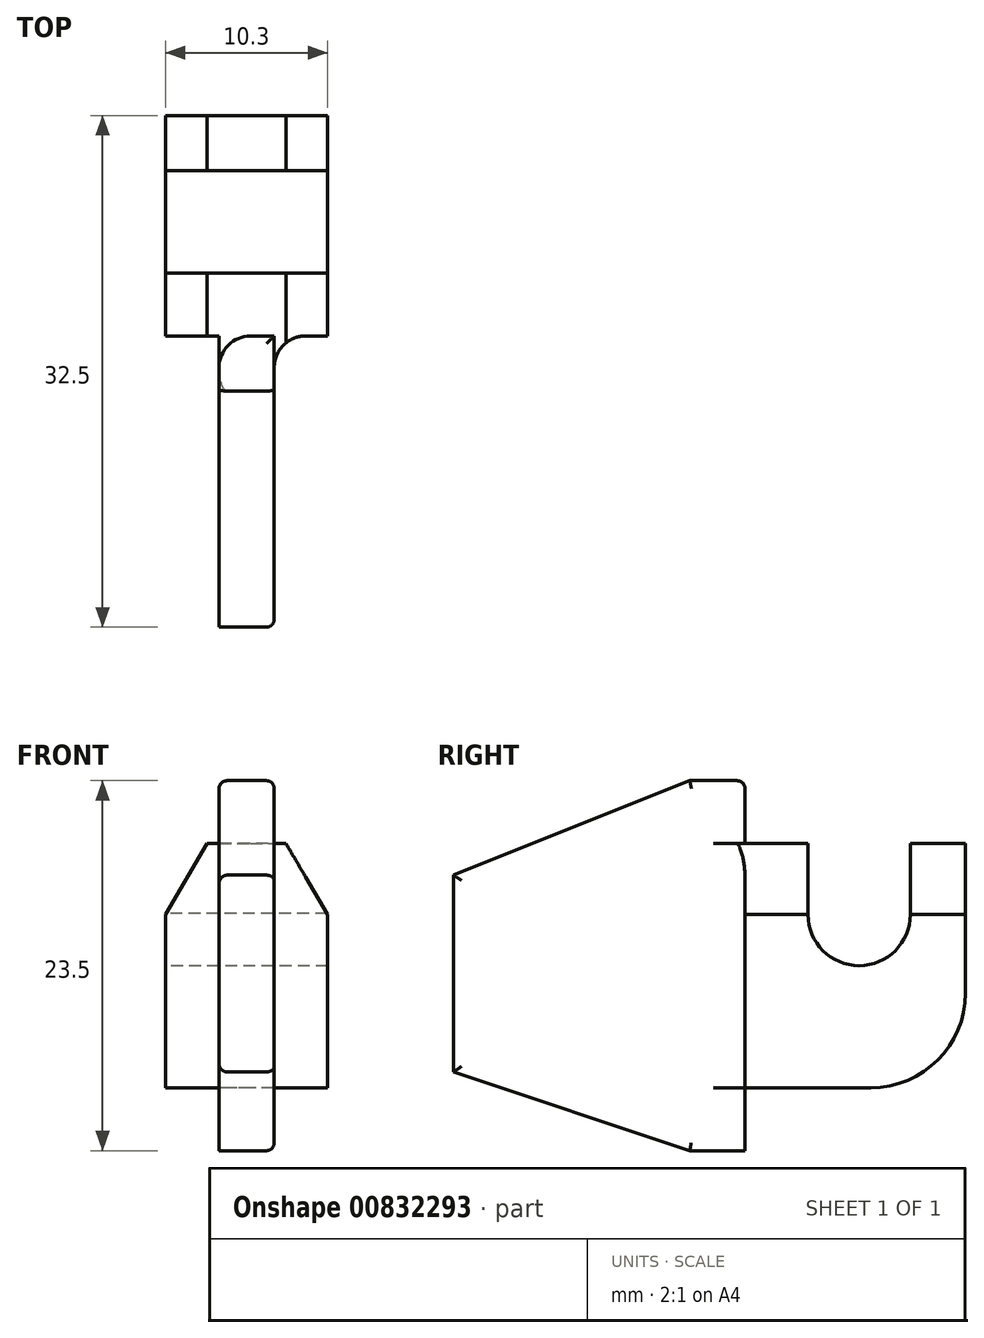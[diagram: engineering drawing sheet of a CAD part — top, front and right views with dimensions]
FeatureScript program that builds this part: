
annotation { "Feature Type Name" : "Feature", "Feature Type Description" : "" }
export const myFeature = defineFeature(function(context is Context, id is Id, definition is map)
    precondition{}
    {
        {
            var Q0;
            Q0=qCreatedBy(makeId("Front.planeOp"),FACE);
            var sketch = newSketch(context, id + "F0", { "sketchPlane" : qUnion([Q0])});
            skLineSegment(sketch, "E0.bottom", {"start": v(5.15, 5.5) * mm, "end": v(-5.15, 5.5) * mm});
            skLineSegment(sketch, "E0.top", {"start": v(5.15, -5.5) * mm, "end": v(-5.15, -5.5) * mm});
            skLineSegment(sketch, "E0.left", {"start": v(5.15, 5.5) * mm, "end": v(5.15, -5.5) * mm});
            skLineSegment(sketch, "E0.right", {"start": v(-5.15, 5.5) * mm, "end": v(-5.15, -5.5) * mm});
            skPoint(sketch, "E0.middle", {"position": v(0, 0) * mm});
            skLineSegment(sketch, "E1", {"start": v(-2.5, 10) * mm, "end": v(2.5, 10) * mm});
            skLineSegment(sketch, "E2", {"start": v(-2.5, 10) * mm, "end": v(-5.15, 5.5) * mm});
            skLineSegment(sketch, "E3", {"start": v(2.5, 10) * mm, "end": v(5.15, 5.5) * mm});
            skLineSegment(sketch, "E4", {"start": v(0, 13.52) * mm, "end": v(0, -10.49) * mm});
            skSolve(sketch);
        }
        {
            var Q0;
            Q0=qSketchRegion(id+"F0",true);
            extrude(context, id + "F1", {"entities" : qUnion([Q0]), "oppositeDirection" : true, "depth" : 14 * mm, "offsetDistance" : 25 * mm});
        }
        {
            var Q0;
            Q0=qCreatedBy(makeId("Right.planeOp"),FACE);
            var sketch = newSketch(context, id + "F2", { "sketchPlane" : qUnion([Q0])});
            skArc(sketch, "E5", {"start": v(4, 5.5) * mm, "mid": v(7.28, 2.25) * mm, "end": v(10.5, 5.57) * mm});
            skLineSegment(sketch, "E6", {"start": v(4, 5.5) * mm, "end": v(4, 10) * mm});
            skLineSegment(sketch, "E7", {"start": v(4, 10) * mm, "end": v(10.5, 10) * mm});
            skLineSegment(sketch, "E8", {"start": v(10.5, 10) * mm, "end": v(10.5, 5.57) * mm});
            skSolve(sketch);
        }
        {
            var Q0;
            Q0=qSketchRegion(id+"F2",true);
            extrude(context, id + "F3", {"entities" : qUnion([Q0]), "operationType" : NewBodyOperationType.REMOVE, "endBound" : BoundingType.THROUGH_ALL, "depth" : 25 * mm, "hasOffset" : true, "offsetDistance" : 50 * mm, "hasSecondDirection" : true, "secondDirectionBound" : SecondDirectionBoundingType.THROUGH_ALL, "secondDirectionOppositeDirection" : true, "secondDirectionDepth" : 50 * mm});
        }
        {
            var Q0;
            Q0=qCreatedBy(makeId("Right.planeOp"),FACE);
            var sketch = newSketch(context, id + "F4", { "sketchPlane" : qUnion([Q0])});
            skLineSegment(sketch, "E9", {"start": v(0, 0) * mm, "end": v(0, 14) * mm});
            skLineSegment(sketch, "E10", {"start": v(0, 14) * mm, "end": v(-3.5, 14) * mm});
            skLineSegment(sketch, "E11", {"start": v(0, 0) * mm, "end": v(0, -9.5) * mm});
            skLineSegment(sketch, "E12", {"start": v(0, -9.5) * mm, "end": v(-3.5, -9.5) * mm});
            skLineSegment(sketch, "E13", {"start": v(-18.5, -4.5) * mm, "end": v(-18.5, 8) * mm});
            skLineSegment(sketch, "E14", {"start": v(-18.5, -4.5) * mm, "end": v(-3.5, -9.5) * mm});
            skLineSegment(sketch, "E15", {"start": v(-18.5, 8) * mm, "end": v(-3.5, 14) * mm});
            skSolve(sketch);
        }
        {
            var Q0;
            Q0=qSketchRegion(id+"F4",true);
            extrude(context, id + "F5", {"entities" : qUnion([Q0]), "operationType" : NewBodyOperationType.ADD, "endBound" : BoundingType.SYMMETRIC, "depth" : 3.5 * mm, "offsetDistance" : 25 * mm});
        }
        {
            var Q0;
            Q0=makeQuery(id+"F1.opExtrude","CAP_EDGE",EDGE,{"disambiguationData":[OSD([sQuery(id+"F0.wireOp",EDGE,"E0.top")])],"isStart":false});
            fillet(context, id + "F6", {"entities" : qUnion([Q0]), "radius" : 6 * mm, "tangentPropagation" : true, "allowEdgeOverflow" : false});
        }
        {
            var Q0;
            {var subQ0=sQuery(id+"F4.wireOp",EDGE,"E11");var subQ1=sQuery(id+"F4.wireOp",EDGE,"E9");Q0=makeQuery(id+"F5.boolean.opBoolean","SPLIT",EDGE,{"disambiguationData":[topologyDisambiguationEdgeConnected([makeQuery(id+"F1.opExtrude","CAP_FACE",FACE,{"disambiguationData":[OSD([sQuery(id+"F0.wireOp",EDGE,"E0.top"),sQuery(id+"F0.wireOp",EDGE,"E0.left"),sQuery(id+"F0.wireOp",EDGE,"E0.right"),sQuery(id+"F0.wireOp",EDGE,"E1"),sQuery(id+"F0.wireOp",EDGE,"E2"),sQuery(id+"F0.wireOp",EDGE,"E3")])],"isStart":true}),makeQuery(id+"F5.opExtrude","CAP_FACE",FACE,{"disambiguationData":[OSD([subQ1,sQuery(id+"F4.wireOp",EDGE,"E10"),subQ0,sQuery(id+"F4.wireOp",EDGE,"E12"),sQuery(id+"F4.wireOp",EDGE,"E13"),sQuery(id+"F4.wireOp",EDGE,"E14"),sQuery(id+"F4.wireOp",EDGE,"E15")])],"isStart":false})])],"derivedFrom":makeQuery(id+"F5.opExtrude","CAP_EDGE",EDGE,{"disambiguationData":[OSD([subQ1,subQ0])],"isStart":false})});}
            var Q1;
            {var subQ0=sQuery(id+"F4.wireOp",EDGE,"E11");var subQ1=sQuery(id+"F4.wireOp",EDGE,"E9");Q1=makeQuery(id+"F5.boolean.opBoolean","SPLIT",EDGE,{"disambiguationData":[topologyDisambiguationEdgeConnected([makeQuery(id+"F1.opExtrude","CAP_FACE",FACE,{"disambiguationData":[OSD([sQuery(id+"F0.wireOp",EDGE,"E0.top"),sQuery(id+"F0.wireOp",EDGE,"E0.left"),sQuery(id+"F0.wireOp",EDGE,"E0.right"),sQuery(id+"F0.wireOp",EDGE,"E1"),sQuery(id+"F0.wireOp",EDGE,"E2"),sQuery(id+"F0.wireOp",EDGE,"E3")])],"isStart":true}),makeQuery(id+"F5.opExtrude","CAP_FACE",FACE,{"disambiguationData":[OSD([subQ1,sQuery(id+"F4.wireOp",EDGE,"E10"),subQ0,sQuery(id+"F4.wireOp",EDGE,"E12"),sQuery(id+"F4.wireOp",EDGE,"E13"),sQuery(id+"F4.wireOp",EDGE,"E14"),sQuery(id+"F4.wireOp",EDGE,"E15")])],"isStart":true})])],"derivedFrom":makeQuery(id+"F5.opExtrude","CAP_EDGE",EDGE,{"disambiguationData":[OSD([subQ1,subQ0])],"isStart":true})});}
            fillet(context, id + "F7", {"entities" : qUnion([Q0, Q1]), "radius" : 2 * mm, "tangentPropagation" : true, "allowEdgeOverflow" : false});
        }
        {
            var Q0;
            Q0=makeQuery(id+"F5.opExtrude","CAP_EDGE",EDGE,{"disambiguationData":[OSD([sQuery(id+"F4.wireOp",EDGE,"E15")])],"isStart":false});
            var Q1;
            Q1=makeQuery(id+"F5.opExtrude","CAP_EDGE",EDGE,{"disambiguationData":[OSD([sQuery(id+"F4.wireOp",EDGE,"E10")])],"isStart":false});
            var Q2;
            Q2=makeQuery(id+"F5.opExtrude","CAP_EDGE",EDGE,{"disambiguationData":[OSD([sQuery(id+"F4.wireOp",EDGE,"E13")])],"isStart":false});
            var Q3;
            Q3=makeQuery(id+"F5.opExtrude","CAP_EDGE",EDGE,{"disambiguationData":[OSD([sQuery(id+"F4.wireOp",EDGE,"E14")])],"isStart":false});
            var Q4;
            Q4=makeQuery(id+"F5.opExtrude","CAP_EDGE",EDGE,{"disambiguationData":[OSD([sQuery(id+"F4.wireOp",EDGE,"E12")])],"isStart":false});
            var Q5;
            Q5=makeQuery(id+"F5.opExtrude","CAP_EDGE",EDGE,{"disambiguationData":[OSD([sQuery(id+"F4.wireOp",EDGE,"E15")])],"isStart":true});
            var Q6;
            Q6=makeQuery(id+"F5.opExtrude","CAP_EDGE",EDGE,{"disambiguationData":[OSD([sQuery(id+"F4.wireOp",EDGE,"E10")])],"isStart":true});
            var Q7;
            Q7=makeQuery(id+"F5.opExtrude","CAP_EDGE",EDGE,{"disambiguationData":[OSD([sQuery(id+"F4.wireOp",EDGE,"E14")])],"isStart":true});
            fillet(context, id + "F8", {"entities" : qUnion([Q0, Q1, Q2, Q3, Q4, Q5, Q6, Q7]), "radius" : .5 * mm, "tangentPropagation" : true, "allowEdgeOverflow" : false});
        }
    });
